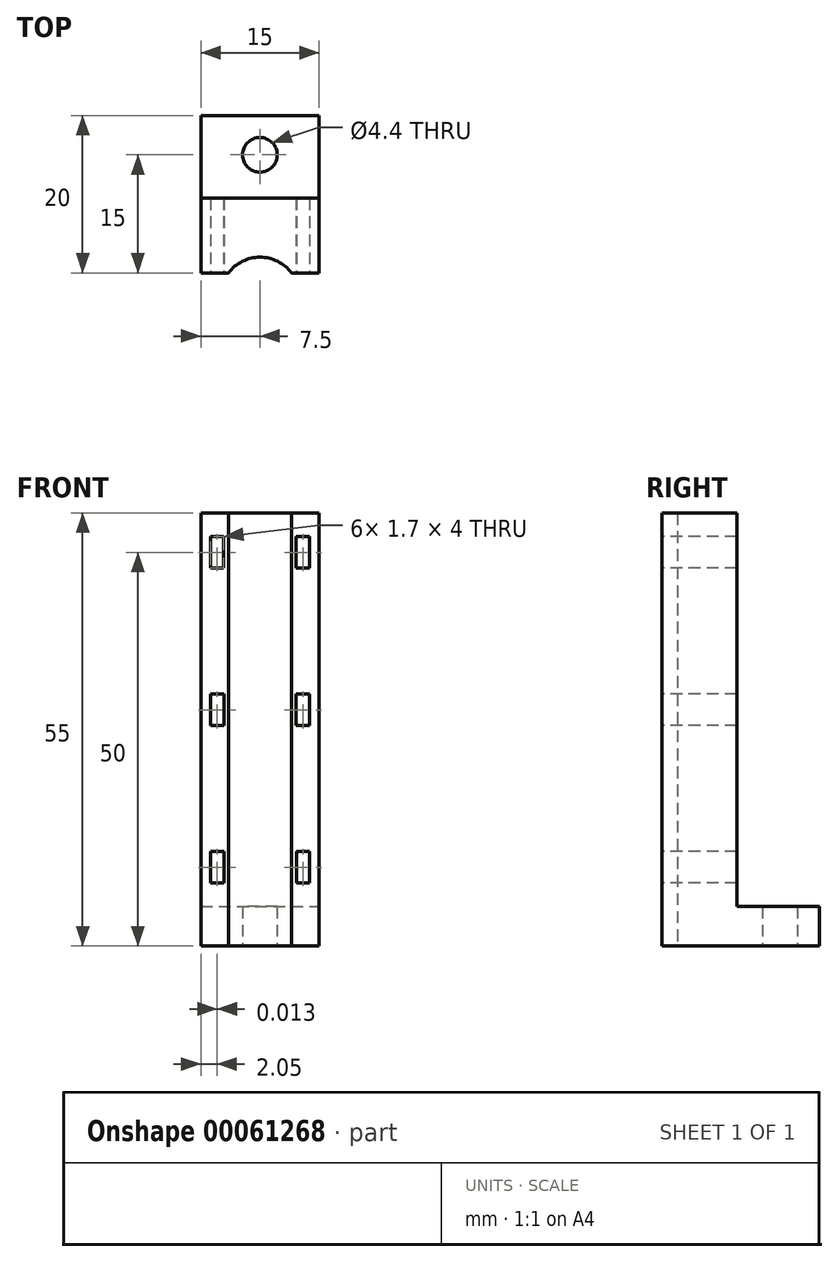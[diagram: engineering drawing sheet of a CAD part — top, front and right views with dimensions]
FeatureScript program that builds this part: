
annotation { "Feature Type Name" : "Feature", "Feature Type Description" : "" }
export const myFeature = defineFeature(function(context is Context, id is Id, definition is map)
    precondition{}
    {
        {
            var Q0;
            Q0=qCreatedBy(makeId("Top.planeOp"),FACE);
            var sketch = newSketch(context, id + "F0", { "sketchPlane" : qUnion([Q0])});
            skLineSegment(sketch, "E0.bottom", {"start": v(0, 0) * mm, "end": v(15, 0) * mm});
            skLineSegment(sketch, "E0.top", {"start": v(0, 20) * mm, "end": v(15, 20) * mm});
            skLineSegment(sketch, "E0.left", {"start": v(0, 0) * mm, "end": v(0, 20) * mm});
            skLineSegment(sketch, "E0.right", {"start": v(15, 0) * mm, "end": v(15, 20) * mm});
            skLineSegment(sketch, "E1", {"start": v(-6.01, 15) * mm, "end": v(39.17, 15) * mm, "construction": true});
            skCircle(sketch, "E2", {"center": v(7.5, 15) * mm, "radius": 2.2 * mm});
            skSolve(sketch);
        }
        {
            var Q0;
            Q0 = qSketchRegion(id + "F0", true);
            extrude(context, id + "F1", {"entities" : qUnion([Q0]), "depth" : 5 * mm});
        }
        {
            var Q0;
            Q0=makeQuery(id+"F1.opExtrude","CAP_FACE",FACE,{"disambiguationData":[OSD([sQuery(id+"F0.wireOp",EDGE,"E0.bottom"),sQuery(id+"F0.wireOp",EDGE,"E0.top"),sQuery(id+"F0.wireOp",EDGE,"E0.left"),sQuery(id+"F0.wireOp",EDGE,"E0.right"),sQuery(id+"F0.wireOp",EDGE,"E2")])],"isStart":false});
            var sketch = newSketch(context, id + "F2", { "sketchPlane" : qUnion([Q0])});
            skArc(sketch, "E3", {"start": v(11.5, 0) * mm, "mid": v(7.5, 2) * mm, "end": v(3.5, 0) * mm});
            skLineSegment(sketch, "E4", {"start": v(3.5, 0) * mm, "end": v(11.5, 0) * mm});
            skSolve(sketch);
        }
        {
            var Q0;
            {var subQ2=sQuery(id+"F2.wireOp",EDGE,"E3");Q0=makeQuery(id+"F2.imprint","IMPRINT",FACE,{"disambiguationData":[TD([[makeQuery(id+"F2.imprint","IMPRINT",EDGE,{"derivedFrom":subQ2}),-1.0]])]});}
            var sketch = newSketch(context, id + "F3", { "sketchPlane" : qUnion([Q0])});
            skLineSegment(sketch, "E5.bottom", {"start": v(0, 0) * mm, "end": v(15, 0) * mm});
            skLineSegment(sketch, "E5.top", {"start": v(0, 9.5) * mm, "end": v(15, 9.5) * mm});
            skLineSegment(sketch, "E5.left", {"start": v(0, 0) * mm, "end": v(0, 9.5) * mm});
            skLineSegment(sketch, "E5.right", {"start": v(15, 0) * mm, "end": v(15, 9.5) * mm});
            skSolve(sketch);
        }
        {
            var Q0;
            Q0 = qSketchRegion(id + "F3", true);
            extrude(context, id + "F4", {"entities" : qUnion([Q0]), "operationType" : NewBodyOperationType.ADD, "depth" : 50 * mm});
        }
        {
            var Q0;
            Q0 = qSketchRegion(id + "F2", true);
            extrude(context, id + "F5", {"entities" : qUnion([Q0]), "operationType" : NewBodyOperationType.REMOVE, "endBound" : BoundingType.SYMMETRIC, "depth" : 100 * mm});
        }
        {
            var Q0;
            {var subQ1=sQuery(id+"F3.wireOp",EDGE,"E5.bottom");var subQ2=sQuery(id+"F0.wireOp",EDGE,"E0.left");var subQ3=sQuery(id+"F0.wireOp",EDGE,"E0.bottom");Q0=makeQuery(id+"F5.boolean.opBoolean","SPLIT",FACE,{"disambiguationData":[TD([makeQuery(id+"F1.opExtrude","SWEPT_FACE",FACE,{"disambiguationData":[OSD([subQ2])]})])],"derivedFrom":makeQuery(id+"F4.boolean.opBoolean","MERGE",FACE,{"derivedFrom":[makeQuery(id+"F1.opExtrude","SWEPT_FACE",FACE,{"disambiguationData":[OSD([subQ3])]}),makeQuery(id+"F4.opExtrude","SWEPT_FACE",FACE,{"disambiguationData":[OSD([subQ1])]})]})});}
            var sketch = newSketch(context, id + "F6", { "sketchPlane" : qUnion([Q0])});
            skLineSegment(sketch, "E6.bottom", {"start": v(1.2, 52) * mm, "end": v(2.9, 52) * mm});
            skLineSegment(sketch, "E6.top", {"start": v(1.2, 48) * mm, "end": v(2.9, 48) * mm});
            skLineSegment(sketch, "E6.left", {"start": v(1.2, 52) * mm, "end": v(1.2, 48) * mm});
            skLineSegment(sketch, "E6.right", {"start": v(2.9, 52) * mm, "end": v(2.9, 48) * mm});
            skLineSegment(sketch, "E7.bottom", {"start": v(13.8, 52) * mm, "end": v(12.1, 52) * mm});
            skLineSegment(sketch, "E7.top", {"start": v(13.8, 48) * mm, "end": v(12.1, 48) * mm});
            skLineSegment(sketch, "E7.left", {"start": v(13.8, 52) * mm, "end": v(13.8, 48) * mm});
            skLineSegment(sketch, "E7.right", {"start": v(12.1, 52) * mm, "end": v(12.1, 48) * mm});
            skLineSegment(sketch, "E8.1.0.0", {"start": v(1.21, 32) * mm, "end": v(1.21, 28) * mm});
            skLineSegment(sketch, "E8.1.0.1", {"start": v(2.91, 32) * mm, "end": v(2.91, 28) * mm});
            skLineSegment(sketch, "E8.1.0.2", {"start": v(1.21, 28) * mm, "end": v(2.91, 28) * mm});
            skLineSegment(sketch, "E8.1.0.3", {"start": v(1.21, 32) * mm, "end": v(2.91, 32) * mm});
            skLineSegment(sketch, "E8.1.0.4", {"start": v(13.81, 32) * mm, "end": v(13.81, 28) * mm});
            skLineSegment(sketch, "E8.1.0.5", {"start": v(12.11, 32) * mm, "end": v(12.11, 28) * mm});
            skLineSegment(sketch, "E8.1.0.6", {"start": v(13.81, 32) * mm, "end": v(12.11, 32) * mm});
            skLineSegment(sketch, "E8.1.0.7", {"start": v(13.81, 28) * mm, "end": v(12.11, 28) * mm});
            skLineSegment(sketch, "E8.2.0.0", {"start": v(1.23, 12) * mm, "end": v(1.23, 8) * mm});
            skLineSegment(sketch, "E8.2.0.1", {"start": v(2.93, 12) * mm, "end": v(2.93, 8) * mm});
            skLineSegment(sketch, "E8.2.0.2", {"start": v(1.23, 8) * mm, "end": v(2.93, 8) * mm});
            skLineSegment(sketch, "E8.2.0.3", {"start": v(1.23, 12) * mm, "end": v(2.93, 12) * mm});
            skLineSegment(sketch, "E8.2.0.4", {"start": v(13.83, 12) * mm, "end": v(13.83, 8) * mm});
            skLineSegment(sketch, "E8.2.0.5", {"start": v(12.13, 12) * mm, "end": v(12.13, 8) * mm});
            skLineSegment(sketch, "E8.2.0.6", {"start": v(13.83, 12) * mm, "end": v(12.13, 12) * mm});
            skLineSegment(sketch, "E8.2.0.7", {"start": v(13.83, 8) * mm, "end": v(12.13, 8) * mm});
            skLineSegment(sketch, "E8.direction1", {"start": v(1.2, 48) * mm, "end": v(1.21, 28) * mm, "construction": true});
            skSolve(sketch);
        }
        {
            var Q0;
            Q0 = qSketchRegion(id + "F6", true);
            extrude(context, id + "F7", {"entities" : qUnion([Q0]), "operationType" : NewBodyOperationType.REMOVE, "oppositeDirection" : true, "depth" : 25 * mm});
        }
    });
